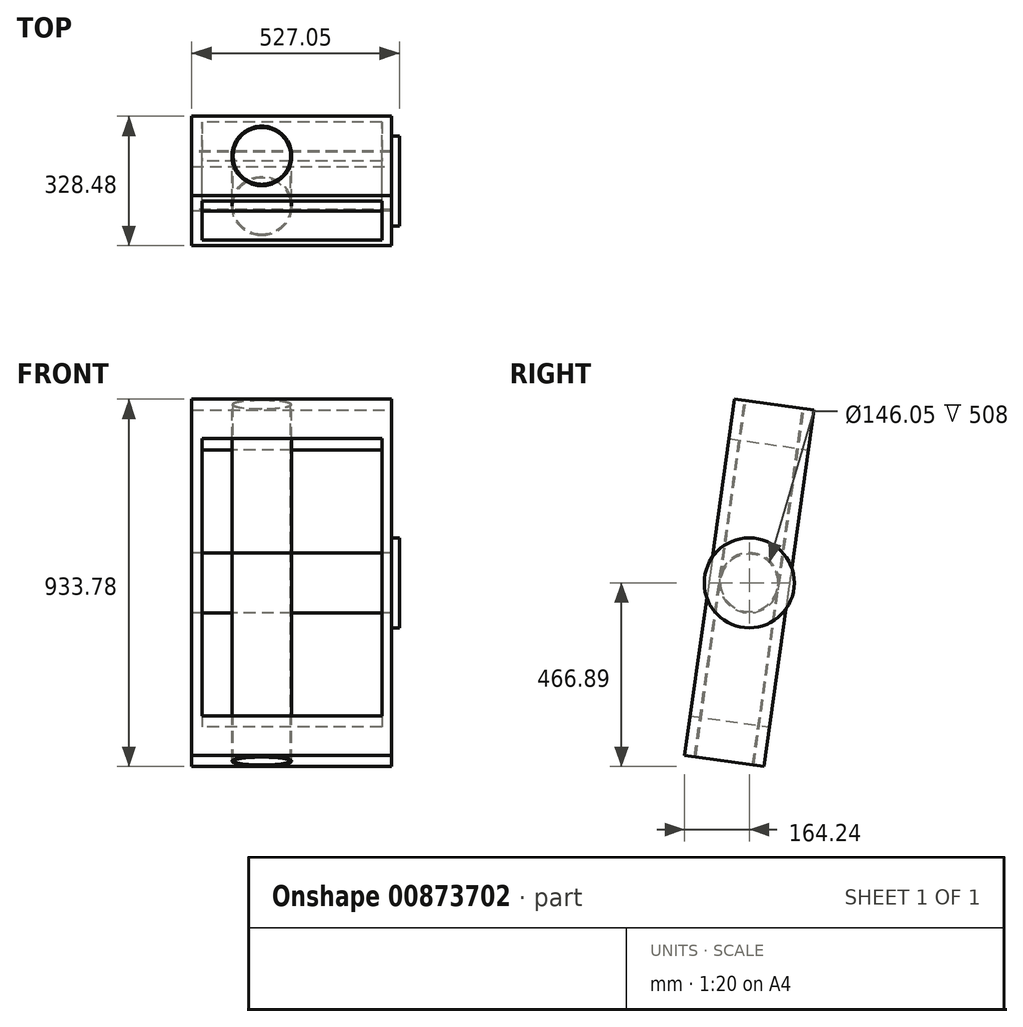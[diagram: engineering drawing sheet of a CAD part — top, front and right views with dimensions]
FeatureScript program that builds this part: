
annotation { "Feature Type Name" : "Feature", "Feature Type Description" : "" }
export const myFeature = defineFeature(function(context is Context, id is Id, definition is map)
    precondition{}
    {
        {
            var Q0;
            Q0=qCreatedBy(makeId("Top.planeOp"),FACE);
            var sketch = newSketch(context, id + "F0", { "sketchPlane" : qUnion([Q0])});
            skLineSegment(sketch, "E0.bottom", {"start": v(-457.2, 254) * mm, "end": v(457.2, 254) * mm});
            skLineSegment(sketch, "E0.top", {"start": v(-457.2, -254) * mm, "end": v(457.2, -254) * mm});
            skLineSegment(sketch, "E0.left", {"start": v(-457.2, 254) * mm, "end": v(-457.2, -254) * mm});
            skLineSegment(sketch, "E0.right", {"start": v(457.2, 254) * mm, "end": v(457.2, -254) * mm});
            skPoint(sketch, "E0.middle", {"position": v(0, 0) * mm});
            skSolve(sketch);
        }
        {
            var Q0;
            Q0 = qSketchRegion(id + "F0", true);
            extrude(context, id + "F1", {"entities" : qUnion([Q0]), "endBound" : BoundingType.SYMMETRIC, "depth" : 203.2 * mm, "offsetDistance" : 25.4 * mm});
        }
        {
            var Q0;
            Q0=makeQuery(id+"F1.opExtrude","CAP_FACE",FACE,{"disambiguationData":[OSD([sQuery(id+"F0.wireOp",EDGE,"E0.bottom"),sQuery(id+"F0.wireOp",EDGE,"E0.top"),sQuery(id+"F0.wireOp",EDGE,"E0.left"),sQuery(id+"F0.wireOp",EDGE,"E0.right")])],"isStart":false});
            var sketch = newSketch(context, id + "F2", { "sketchPlane" : qUnion([Q0])});
            skLineSegment(sketch, "E1.bottom", {"start": v(-355.6, -228.6) * mm, "end": v(355.6, -228.6) * mm});
            skLineSegment(sketch, "E1.top", {"start": v(-355.6, 228.6) * mm, "end": v(355.6, 228.6) * mm});
            skLineSegment(sketch, "E1.left", {"start": v(-355.6, -228.6) * mm, "end": v(-355.6, 228.6) * mm});
            skLineSegment(sketch, "E1.right", {"start": v(355.6, -228.6) * mm, "end": v(355.6, 228.6) * mm});
            skPoint(sketch, "E1.middle", {"position": v(0, 0) * mm});
            skSolve(sketch);
        }
        {
            var Q0;
            Q0=makeQuery(id+"F2.imprint","IMPRINT",FACE,{"disambiguationData":[TD([[makeQuery(id+"F2.imprint","IMPRINT",EDGE,{"derivedFrom":sQuery(id+"F2.wireOp",EDGE,"E1.bottom")}),1.0]])]});
            extrude(context, id + "F3", {"entities" : qUnion([Q0]), "operationType" : NewBodyOperationType.REMOVE, "endBound" : BoundingType.THROUGH_ALL, "oppositeDirection" : true, "depth" : 25.4 * mm, "offsetDistance" : 25.4 * mm});
        }
        {
            var Q0;
            Q0=qCreatedBy(makeId("Front.planeOp"),FACE);
            var sketch = newSketch(context, id + "F4", { "sketchPlane" : qUnion([Q0])});
            skCircle(sketch, "E2", {"center": v(0, 0) * mm, "radius": 76.2 * mm});
            skCircle(sketch, "E3", {"center": v(0, 0) * mm, "radius": 73.03 * mm});
            skSolve(sketch);
        }
        {
            var Q0;
            Q0 = qSketchRegion(id + "F4", true);
            extrude(context, id + "F5", {"entities" : qUnion([Q0]), "endBound" : BoundingType.SYMMETRIC, "depth" : 508 * mm, "offsetDistance" : 25.4 * mm});
        }
        {
            var Q0;
            Q0=qCreatedBy(makeId("Right.planeOp"),FACE);
            var sketch = newSketch(context, id + "F6", { "sketchPlane" : qUnion([Q0])});
            skCircle(sketch, "E4", {"center": v(0, 0) * mm, "radius": 76.2 * mm});
            skCircle(sketch, "E5", {"center": v(0, 0) * mm, "radius": 73.03 * mm});
            skSolve(sketch);
        }
        {
            var Q0;
            Q0 = qSketchRegion(id + "F6", true);
            extrude(context, id + "F7", {"entities" : qUnion([Q0]), "endBound" : BoundingType.SYMMETRIC, "depth" : 914.4 * mm, "offsetDistance" : 25.4 * mm});
        }
        {
            var Q0;
            Q0=makeQuery(id+"F7.opExtrude","SWEPT_BODY",BODY,{"disambiguationData":[OSD([sQuery(id+"F6.wireOp",EDGE,"E4"),sQuery(id+"F6.wireOp",EDGE,"E5")])]});
            var Q1;
            Q1=makeQuery(id+"F1.opExtrude","SWEPT_BODY",BODY,{"disambiguationData":[OSD([sQuery(id+"F0.wireOp",EDGE,"E0.bottom"),sQuery(id+"F0.wireOp",EDGE,"E0.top"),sQuery(id+"F0.wireOp",EDGE,"E0.left"),sQuery(id+"F0.wireOp",EDGE,"E0.right")])]});
            var Q2;
            Q2=makeQuery(id+"F5.opExtrude","SWEPT_BODY",BODY,{"disambiguationData":[OSD([sQuery(id+"F4.wireOp",EDGE,"E2"),sQuery(id+"F4.wireOp",EDGE,"E3")])]});
            var Q3;
            Q3=makeQuery(id+"F5.opExtrude","SWEPT_FACE",FACE,{"disambiguationData":[OSD([sQuery(id+"F4.wireOp",EDGE,"E2")])]});
            transform(context, id + "F8", {"entities" : qUnion([Q0, Q1, Q2]), "transformType" : TransformType.ROTATION, "transformAxis" : qUnion([Q3]), "angle" : 90 * degree, "makeCopy" : false});
        }
        {
            var Q0;
            Q0=makeQuery(id+"F1.opExtrude","SWEPT_BODY",BODY,{"disambiguationData":[OSD([sQuery(id+"F0.wireOp",EDGE,"E0.bottom"),sQuery(id+"F0.wireOp",EDGE,"E0.top"),sQuery(id+"F0.wireOp",EDGE,"E0.left"),sQuery(id+"F0.wireOp",EDGE,"E0.right")])]});
            var Q1;
            Q1=makeQuery(id+"F5.opExtrude","SWEPT_BODY",BODY,{"disambiguationData":[OSD([sQuery(id+"F4.wireOp",EDGE,"E2"),sQuery(id+"F4.wireOp",EDGE,"E3")])]});
            var Q2;
            Q2=makeQuery(id+"F7.opExtrude","SWEPT_BODY",BODY,{"disambiguationData":[OSD([sQuery(id+"F6.wireOp",EDGE,"E4"),sQuery(id+"F6.wireOp",EDGE,"E5")])]});
            var Q3;
            Q3=makeQuery(id+"F7.opExtrude","SWEPT_FACE",FACE,{"disambiguationData":[OSD([sQuery(id+"F6.wireOp",EDGE,"E4")])]});
            transform(context, id + "F9", {"entities" : qUnion([Q0, Q1, Q2]), "transformType" : TransformType.ROTATION, "transformAxis" : qUnion([Q3]), "angle" : 90 * degree, "makeCopy" : false});
        }
        {
            var Q0;
            Q0=makeQuery(id+"F1.opExtrude","SWEPT_BODY",BODY,{"disambiguationData":[OSD([sQuery(id+"F0.wireOp",EDGE,"E0.bottom"),sQuery(id+"F0.wireOp",EDGE,"E0.top"),sQuery(id+"F0.wireOp",EDGE,"E0.left"),sQuery(id+"F0.wireOp",EDGE,"E0.right")])]});
            var Q1;
            Q1=makeQuery(id+"F5.opExtrude","SWEPT_BODY",BODY,{"disambiguationData":[OSD([sQuery(id+"F4.wireOp",EDGE,"E2"),sQuery(id+"F4.wireOp",EDGE,"E3")])]});
            var Q2;
            Q2=makeQuery(id+"F7.opExtrude","SWEPT_BODY",BODY,{"disambiguationData":[OSD([sQuery(id+"F6.wireOp",EDGE,"E4"),sQuery(id+"F6.wireOp",EDGE,"E5")])]});
            var Q3;
            Q3=makeQuery(id+"F5.opExtrude","SWEPT_FACE",FACE,{"disambiguationData":[OSD([sQuery(id+"F4.wireOp",EDGE,"E2")])]});
            transform(context, id + "F10", {"entities" : qUnion([Q0, Q1, Q2]), "transformType" : TransformType.ROTATION, "transformAxis" : qUnion([Q3]), "angle" : 8 * degree, "makeCopy" : false});
        }
        {
            var Q0;
            Q0=makeQuery(id+"F1.opExtrude","SWEPT_BODY",BODY,{"disambiguationData":[OSD([sQuery(id+"F0.wireOp",EDGE,"E0.bottom"),sQuery(id+"F0.wireOp",EDGE,"E0.top"),sQuery(id+"F0.wireOp",EDGE,"E0.left"),sQuery(id+"F0.wireOp",EDGE,"E0.right")])]});
            var Q1;
            Q1=makeQuery(id+"F5.opExtrude","SWEPT_BODY",BODY,{"disambiguationData":[OSD([sQuery(id+"F4.wireOp",EDGE,"E2"),sQuery(id+"F4.wireOp",EDGE,"E3")])]});
            var Q2;
            Q2=makeQuery(id+"F7.opExtrude","SWEPT_BODY",BODY,{"disambiguationData":[OSD([sQuery(id+"F6.wireOp",EDGE,"E4"),sQuery(id+"F6.wireOp",EDGE,"E5")])]});
            transform(context, id + "F11", {"entities" : qUnion([Q0, Q1, Q2]), "transformType" : TransformType.TRANSLATION_3D, "dx" : 76.2 * mm, "dy" : 0 * mm, "dz" : 0 * mm, "makeCopy" : false});
        }
        {
            var Q0;
            Q0=makeQuery(id+"F7.opExtrude","SWEPT_BODY",BODY,{"disambiguationData":[OSD([sQuery(id+"F6.wireOp",EDGE,"E4"),sQuery(id+"F6.wireOp",EDGE,"E5")])]});
            transform(context, id + "F12", {"entities" : qUnion([Q0]), "transformType" : TransformType.TRANSLATION_3D, "dx" : -76.2 * mm, "dy" : 0 * mm, "dz" : 0 * mm, "makeCopy" : false});
        }
        {
            var Q0;
            Q0=makeQuery(id+"F1.opExtrude","SWEPT_FACE",FACE,{"disambiguationData":[OSD([sQuery(id+"F0.wireOp",EDGE,"E0.top")])]});
            var sketch = newSketch(context, id + "F13", { "sketchPlane" : qUnion([Q0])});
            skCircle(sketch, "E6", {"center": v(0, 0) * mm, "radius": 114.3 * mm});
            skSolve(sketch);
        }
        {
            var Q0;
            Q0 = qSketchRegion(id + "F13", true);
            extrude(context, id + "F14", {"entities" : qUnion([Q0]), "depth" : 19.05 * mm, "offsetDistance" : 25.4 * mm});
        }
    });
